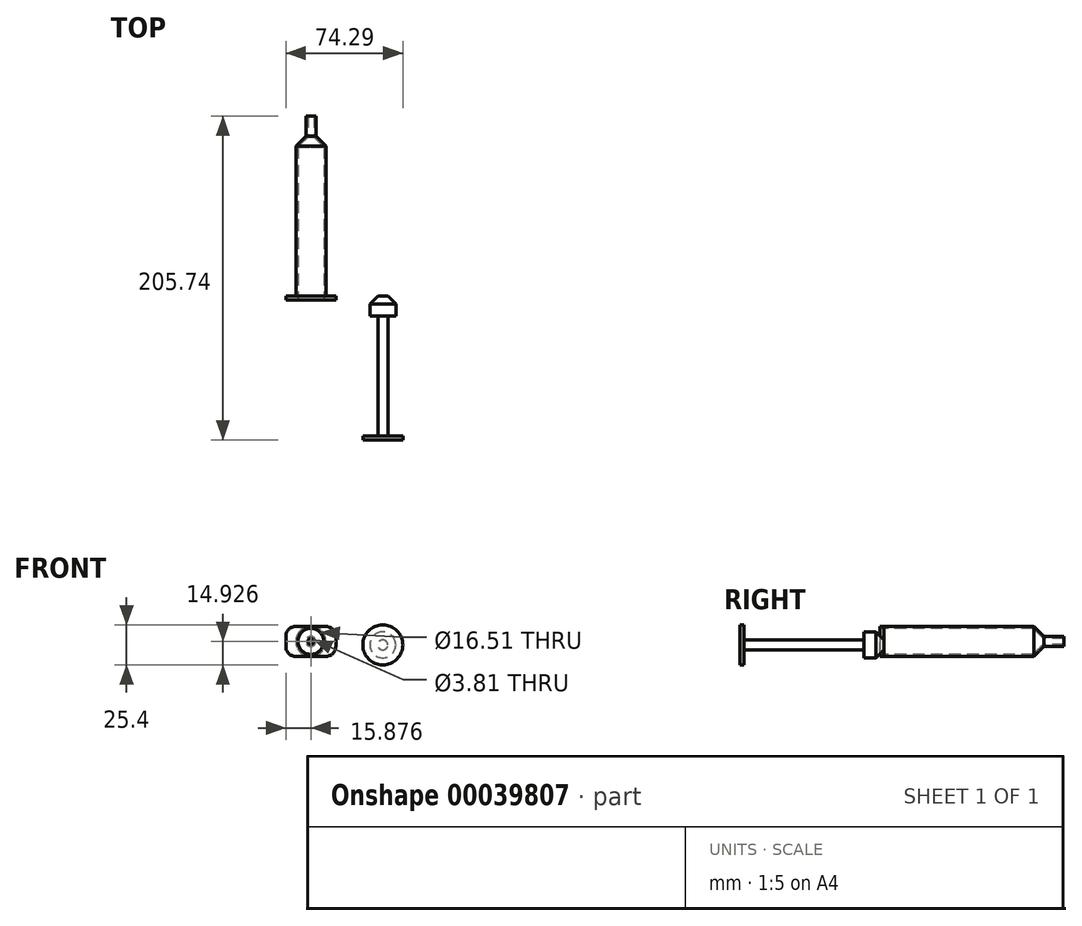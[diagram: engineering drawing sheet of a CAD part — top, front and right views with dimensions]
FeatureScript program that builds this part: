
annotation { "Feature Type Name" : "Feature", "Feature Type Description" : "" }
export const myFeature = defineFeature(function(context is Context, id is Id, definition is map)
    precondition{}
    {
        {
            var Q0;
            Q0=qCreatedBy(makeId("Front.planeOp"),FACE);
            var sketch = newSketch(context, id + "F0", { "sketchPlane" : qUnion([Q0])});
            skCircle(sketch, "E0", {"center": v(-23.42, 17.14) * mm, "radius": 9.53 * mm});
            skSolve(sketch);
        }
        {
            var Q0;
            Q0=makeQuery(id+"F0.imprint","IMPRINT",FACE,{"disambiguationData":[TD([[makeQuery(id+"F0.imprint","IMPRINT",EDGE,{"derivedFrom":sQuery(id+"F0.wireOp",EDGE,"E0")}),1.0]])]});
            extrude(context, id + "F1", {"entities" : qUnion([Q0]), "oppositeDirection" : true, "depth" : 101.6 * mm});
        }
        {
            var Q0;
            Q0=makeQuery(id+"F1.opExtrude","CAP_EDGE",EDGE,{"disambiguationData":[OSD([sQuery(id+"F0.wireOp",EDGE,"E0")])],"isStart":false});
            chamfer(context, id + "F2", {"entities" : qUnion([Q0]), "width" : 6.35 * mm, "tangentPropagation" : true});
        }
        {
            var Q0;
            Q0=makeQuery(id+"F1.opExtrude","CAP_FACE",FACE,{"disambiguationData":[OSD([sQuery(id+"F0.wireOp",EDGE,"E0")])],"isStart":false});
            extrude(context, id + "F3", {"entities" : qUnion([Q0]), "operationType" : NewBodyOperationType.ADD, "depth" : 12.7 * mm});
        }
        {
            var Q0;
            Q0=makeQuery(id+"F1.opExtrude","CAP_FACE",FACE,{"disambiguationData":[OSD([sQuery(id+"F0.wireOp",EDGE,"E0")])],"isStart":true});
            shell(context, id + "F4", {"entities" : qUnion([Q0]), "thickness" : 1.27 * mm});
        }
        {
            var Q0;
            {var subQ0=sQuery(id+"F0.wireOp",EDGE,"E0");Q0=makeQuery(id+"F4.opShell","OFFSET_FACE",FACE,{"disambiguationData":[OSD([subQ0]),TDD([makeQuery(id+"F3.opExtrude","CAP_FACE",FACE,{"disambiguationData":[OSD([subQ0])],"isStart":false})])]});}
            extrude(context, id + "F5", {"entities" : qUnion([Q0]), "operationType" : NewBodyOperationType.REMOVE, "oppositeDirection" : true, "depth" : 25.4 * mm});
        }
        {
            var Q0;
            Q0=makeQuery(id+"F1.opExtrude","CAP_FACE",FACE,{"disambiguationData":[OSD([sQuery(id+"F0.wireOp",EDGE,"E0")])],"isStart":true});
            var sketch = newSketch(context, id + "F6", { "sketchPlane" : qUnion([Q0])});
            skLineSegment(sketch, "E1.rect.bottom", {"start": v(-39.3, 26.66) * mm, "end": v(-7.55, 26.66) * mm});
            skLineSegment(sketch, "E1.rect.top", {"start": v(-39.3, 7.61) * mm, "end": v(-7.55, 7.61) * mm});
            skLineSegment(sketch, "E1.rect.left", {"start": v(-39.3, 26.66) * mm, "end": v(-39.3, 7.61) * mm});
            skLineSegment(sketch, "E1.rect.right", {"start": v(-7.55, 26.66) * mm, "end": v(-7.55, 7.61) * mm});
            skPoint(sketch, "E1.rect.middle", {"position": v(-23.42, 17.14) * mm});
            skSolve(sketch);
        }
        {
            var Q0;
            {var subQ5=sQuery(id+"F6.wireOp",EDGE,"E1.rect.left");Q0=makeQuery(id+"F6.imprint","IMPRINT",FACE,{"disambiguationData":[TD([[makeQuery(id+"F6.imprint","IMPRINT",EDGE,{"derivedFrom":subQ5}),1.0]])]});}
            var Q1;
            {var subQ5=sQuery(id+"F6.wireOp",EDGE,"E1.rect.right");Q1=makeQuery(id+"F6.imprint","IMPRINT",FACE,{"disambiguationData":[TD([[makeQuery(id+"F6.imprint","IMPRINT",EDGE,{"derivedFrom":subQ5}),-1.0]])]});}
            var Q2;
            {var subQ0=sQuery(id+"F0.wireOp",EDGE,"E0");var subQ1=makeQuery(id+"F1.opExtrude","CAP_EDGE",EDGE,{"disambiguationData":[OSD([subQ0])],"isStart":true});Q2=makeQuery(id+"F6.imprint","IMPRINT",FACE,{"disambiguationData":[TD([[makeQuery(id+"F6.imprint","IMPRINT",EDGE,{"derivedFrom":makeQuery(id+"F4.opShell","OFFSET_EDGE",EDGE,{"disambiguationData":[OSD([subQ0]),TDD([subQ1])]})}),-1.0]])]});}
            extrude(context, id + "F7", {"entities" : qUnion([Q0, Q1, Q2]), "operationType" : NewBodyOperationType.ADD, "depth" : 2.54 * mm});
        }
        {
            var Q0;
            Q0=makeQuery(id+"F7.opExtrude","SWEPT_EDGE",EDGE,{"disambiguationData":[OSD([sQuery(id+"F6.wireOp",EDGE,"E1.rect.bottom"),sQuery(id+"F6.wireOp",EDGE,"E1.rect.left")])]});
            var Q1;
            Q1=makeQuery(id+"F7.opExtrude","SWEPT_EDGE",EDGE,{"disambiguationData":[OSD([sQuery(id+"F6.wireOp",EDGE,"E1.rect.top"),sQuery(id+"F6.wireOp",EDGE,"E1.rect.left")])]});
            var Q2;
            Q2=makeQuery(id+"F7.opExtrude","SWEPT_EDGE",EDGE,{"disambiguationData":[OSD([sQuery(id+"F6.wireOp",EDGE,"E1.rect.bottom"),sQuery(id+"F6.wireOp",EDGE,"E1.rect.right")])]});
            var Q3;
            Q3=makeQuery(id+"F7.opExtrude","SWEPT_EDGE",EDGE,{"disambiguationData":[OSD([sQuery(id+"F6.wireOp",EDGE,"E1.rect.top"),sQuery(id+"F6.wireOp",EDGE,"E1.rect.right")])]});
            fillet(context, id + "F8", {"entities" : qUnion([Q0, Q1, Q2, Q3]), "radius" : 6.35 * mm, "tangentPropagation" : true, "allowEdgeOverflow" : false});
        }
        {
            var Q0;
            Q0=qCreatedBy(makeId("Front.planeOp"),FACE);
            var sketch = newSketch(context, id + "F9", { "sketchPlane" : qUnion([Q0])});
            skCircle(sketch, "E2", {"center": v(22.29, 14.91) * mm, "radius": 8.26 * mm});
            skSolve(sketch);
        }
        {
            var Q0;
            Q0=makeQuery(id+"F9.imprint","IMPRINT",FACE,{"disambiguationData":[TD([[makeQuery(id+"F9.imprint","IMPRINT",EDGE,{"derivedFrom":sQuery(id+"F9.wireOp",EDGE,"E2")}),1.0]])]});
            extrude(context, id + "F10", {"entities" : qUnion([Q0]), "depth" : 12.7 * mm});
        }
        {
            var Q0;
            Q0=makeQuery(id+"F10.opExtrude","CAP_FACE",FACE,{"disambiguationData":[OSD([sQuery(id+"F9.wireOp",EDGE,"E2")])],"isStart":false});
            var sketch = newSketch(context, id + "F11", { "sketchPlane" : qUnion([Q0])});
            skCircle(sketch, "E3", {"center": v(22.29, 14.91) * mm, "radius": 3.17 * mm});
            skSolve(sketch);
        }
        {
            var Q0;
            Q0=makeQuery(id+"F11.imprint","IMPRINT",FACE,{"disambiguationData":[TD([[makeQuery(id+"F11.imprint","IMPRINT",EDGE,{"derivedFrom":sQuery(id+"F11.wireOp",EDGE,"E3")}),1.0]])]});
            extrude(context, id + "F12", {"entities" : qUnion([Q0]), "operationType" : NewBodyOperationType.ADD, "depth" : 76.2 * mm});
        }
        {
            var Q0;
            Q0=makeQuery(id+"F12.opExtrude","CAP_FACE",FACE,{"disambiguationData":[OSD([sQuery(id+"F11.wireOp",EDGE,"E3")])],"isStart":false});
            var sketch = newSketch(context, id + "F13", { "sketchPlane" : qUnion([Q0])});
            skCircle(sketch, "E4", {"center": v(22.29, 14.91) * mm, "radius": 12.7 * mm});
            skSolve(sketch);
        }
        {
            var Q0;
            Q0=makeQuery(id+"F13.imprint","IMPRINT",FACE,{"disambiguationData":[TD([[makeQuery(id+"F13.imprint","IMPRINT",EDGE,{"derivedFrom":sQuery(id+"F13.wireOp",EDGE,"E4")}),1.0]])]});
            var Q1;
            Q1=makeQuery(id+"F13.imprint","IMPRINT",FACE,{"disambiguationData":[TD([[makeQuery(id+"F13.imprint","IMPRINT",EDGE,{"derivedFrom":makeQuery(id+"F12.opExtrude","CAP_EDGE",EDGE,{"disambiguationData":[OSD([sQuery(id+"F11.wireOp",EDGE,"E3")])],"isStart":false})}),1.0]])]});
            extrude(context, id + "F14", {"entities" : qUnion([Q0, Q1]), "operationType" : NewBodyOperationType.ADD, "depth" : 2.54 * mm});
        }
        {
            var Q0;
            Q0=makeQuery(id+"F10.opExtrude","CAP_EDGE",EDGE,{"disambiguationData":[OSD([sQuery(id+"F9.wireOp",EDGE,"E2")])],"isStart":true});
            chamfer(context, id + "F15", {"entities" : qUnion([Q0]), "width" : 5.08 * mm, "tangentPropagation" : true});
        }
    });
